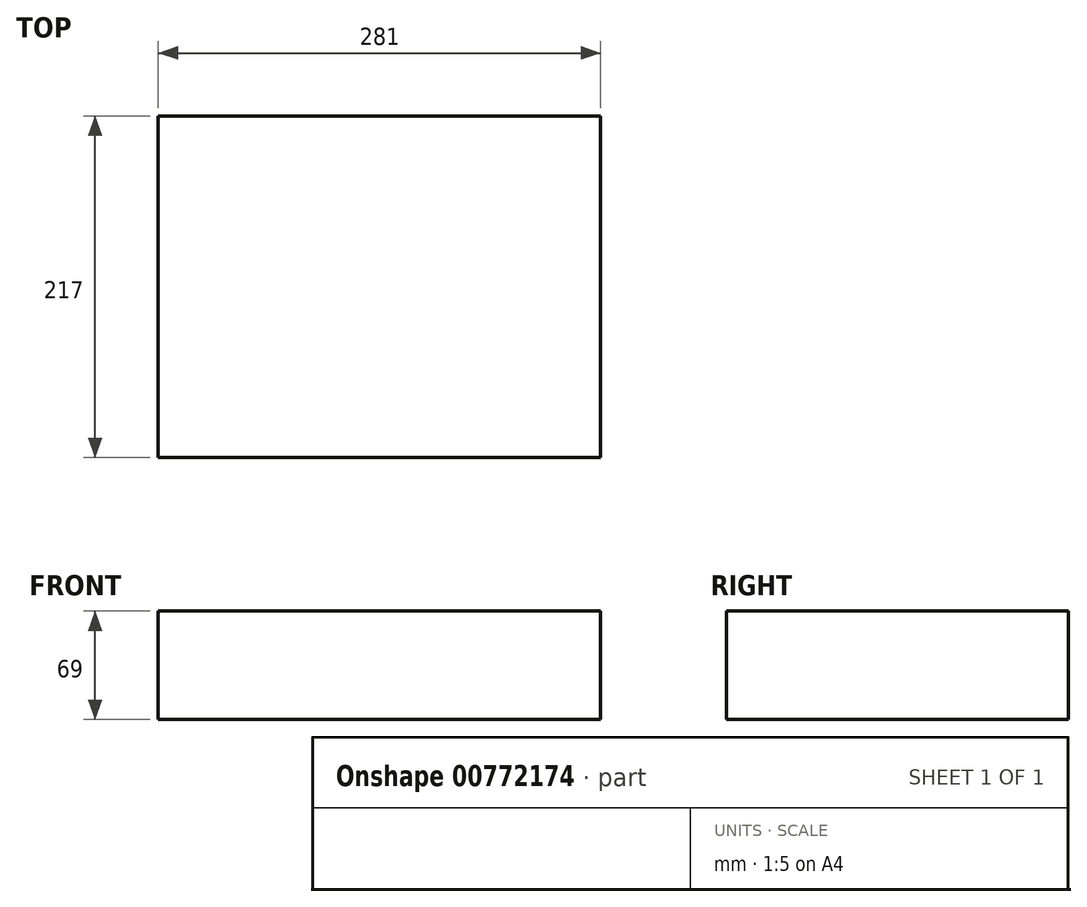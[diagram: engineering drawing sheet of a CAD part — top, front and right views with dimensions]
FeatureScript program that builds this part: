
annotation { "Feature Type Name" : "Feature", "Feature Type Description" : "" }
export const myFeature = defineFeature(function(context is Context, id is Id, definition is map)
    precondition{}
    {
        {
            var Q0;
            Q0=qCreatedBy(makeId("Top.planeOp"),FACE);
            var sketch = newSketch(context, id + "F0", { "sketchPlane" : qUnion([Q0])});
            skLineSegment(sketch, "E0.bottom", {"start": v(140.5, -108.5) * mm, "end": v(-140.5, -108.5) * mm});
            skLineSegment(sketch, "E0.top", {"start": v(140.5, 108.5) * mm, "end": v(-140.5, 108.5) * mm});
            skLineSegment(sketch, "E0.left", {"start": v(140.5, -108.5) * mm, "end": v(140.5, 108.5) * mm});
            skLineSegment(sketch, "E0.right", {"start": v(-140.5, -108.5) * mm, "end": v(-140.5, 108.5) * mm});
            skPoint(sketch, "E0.middle", {"position": v(0, 0) * mm});
            skSolve(sketch);
        }
        {
            var Q0;
            Q0=makeQuery(id+"F0.imprint","IMPRINT",FACE,{"disambiguationData":[TD([[makeQuery(id+"F0.imprint","IMPRINT",EDGE,{"derivedFrom":sQuery(id+"F0.wireOp",EDGE,"E0.bottom")}),-1.0]])]});
            extrude(context, id + "F1", {"entities" : qUnion([Q0]), "depth" : 69 * mm, "offsetDistance" : 25 * mm});
        }
    });
